# Revit family: 2014-Ventana_Uni2_RT-1
name_source: partatom
category: Windows
revit_build: Autodesk Revit 2014 (Build: 20130308_1515(x64)
units: mm (PartAtom-declared; Revit-internal decimal feet)

## types (6) — shared parameters
Acabado = Acabados en anodizado o lacado a cualquier color de la gama ral.
Aislamiento Acústico (dBA) = 27
Aislamiento Térmico (W/m2K) = 3.1
Altura Perfil Marco = 53 mm  [stored 0.173885 ft]
Analytic Construction = Double glazing - domestic
Assembly Code = B2020110
Bimetica = www.bimetica.es
Colección = Línea Clima
Composición del Acristalamiento = Vidrio, Claro Templado 4/16/4
Creado por = Bimetica Parametric Design Services S.L.
Description = Ventana incorpora exclusivo sistema hermético vertical uin2, rotura de puente térmico y la posibilidad de instalar un vidrio de hasta 28 mm. Consta de un área de ventilación de hasta 81%
Fecha Revisión de Contenido = 16/10/2014
Fecha de Caducidad de Información = 01/01/2016
Grosor = 58 mm  [stored 0.190289 ft]
Grosor de Vidrio = 28 mm  [stored 0.0918635 ft]
Heat Transfer Coefficient (U) = 3.1292 W/(m²·K)
IFC Clasificación = Ventana
Información Técnica = http://www.uin2.com
Manufacturer = uin2
Material del Marco = Aluminio
Model = uin2.RT-1
Operation = Ventana Fija
Peso = 0.00 kN
Refuerzo = Acero, Galvanizado
Rotura Puente Térmico = Poliamida
Solar Heat Gain Coefficient = 0.76
Thermal Resistance (R) = 0.3196 (m²·K)/W
UNSPC Categoría = Windows
UNSPC Código = 30171600
URL = http://www.uin2.com
URL Producto = http://www.uin2.com
Uniclass 2.0 Código = 30.00.00
Uniclass 2.0 Descripción = Accessible openings: Doors and hatches, French windows, sliding wall windows.
Visual Light Transmittance = 0.81
Wall Closure = By host
zero-valued in all types: Desfase Exterior, Desfase Interior, Permeabilidad al Aire

## per-type parameters (varying)
| type | Altura de Panel | Apertura | Height | Panel 1 | Panel 2 | Panel 3 | Panel 4 | Panel 5 | Panel 6 | Rough Height | Rough Width | Width |
| 600 x 619 mm | 244 mm | 107 mm  [stored 0.35105 ft] | 619 mm  [stored 2.03084 ft] | Yes | No | No | No | No | No | 631 mm  [stored 2.07021 ft] | 612 mm  [stored 2.00787 ft] | 600 mm |
| 1.200 x 2.011 mm | 313 mm | 142 mm | 2011 mm  [stored 6.59777 ft] | No | Yes | Yes | Yes | Yes | Yes | 2023 mm  [stored 6.63714 ft] | 1212 mm  [stored 3.97638 ft] | 1200 mm |
| 600 x 885 mm | 377 mm | 174 mm | 885 mm | No | Yes | No | No | No | No | 897 mm  [stored 2.94291 ft] | 612 mm  [stored 2.00787 ft] | 600 mm |
| 800 x 1.152 mm | 340 mm | 155 mm | 1152 mm  [stored 3.77953 ft] | No | Yes | Yes | No | No | No | 1164 mm  [stored 3.8189 ft] | 812 mm  [stored 2.66404 ft] | 800 mm  [stored 2.62467 ft] |
| 800 x 1.418 mm | 322 mm | 146 mm | 1418 mm  [stored 4.65223 ft] | No | Yes | Yes | Yes | No | No | 1430 mm  [stored 4.6916 ft] | 812 mm  [stored 2.66404 ft] | 800 mm  [stored 2.62467 ft] |
| 1.000 x 1.692 mm | 312 mm | 141 mm | 1692 mm  [stored 5.55118 ft] | No | Yes | Yes | Yes | Yes | No | 1704 mm  [stored 5.59055 ft] | 1012 mm  [stored 3.32021 ft] | 1000 mm  [stored 3.28084 ft] |

note: [stored X ft] marks values corroborated as IEEE doubles in the binary element streams (Revit-internal decimal feet)

## geometry (parser evidence)
native form markers: Blend x8, Sweep x3
no freeform markers — native parametric forms only
